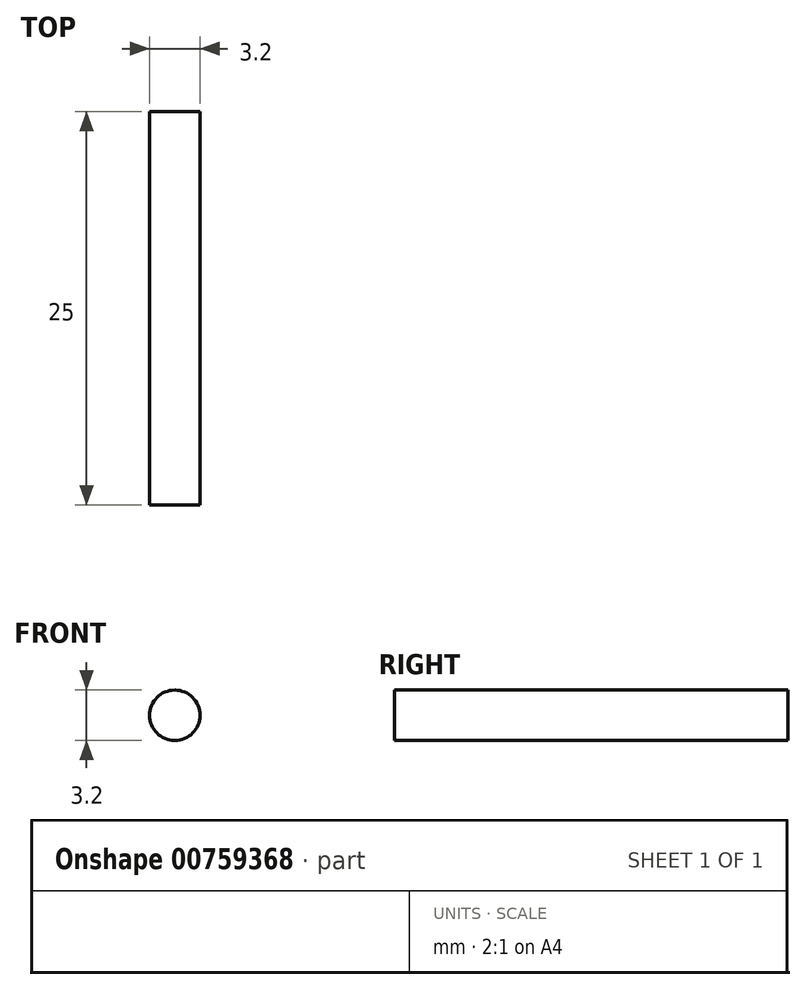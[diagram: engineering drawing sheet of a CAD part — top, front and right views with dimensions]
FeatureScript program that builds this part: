
annotation { "Feature Type Name" : "Feature", "Feature Type Description" : "" }
export const myFeature = defineFeature(function(context is Context, id is Id, definition is map)
    precondition{}
    {
        {
            var Q0;
            Q0=qCreatedBy(makeId("Front.planeOp"),FACE);
            var sketch = newSketch(context, id + "F0", { "sketchPlane" : qUnion([Q0])});
            skCircle(sketch, "E0", {"center": v(0.25, 0) * mm, "radius": 1.6 * mm});
            skSolve(sketch);
        }
        {
            var Q0;
            Q0 = qSketchRegion(id + "F0", true);
            extrude(context, id + "F1", {"entities" : qUnion([Q0]), "depth" : 25 * mm, "offsetDistance" : 25 * mm});
        }
    });
